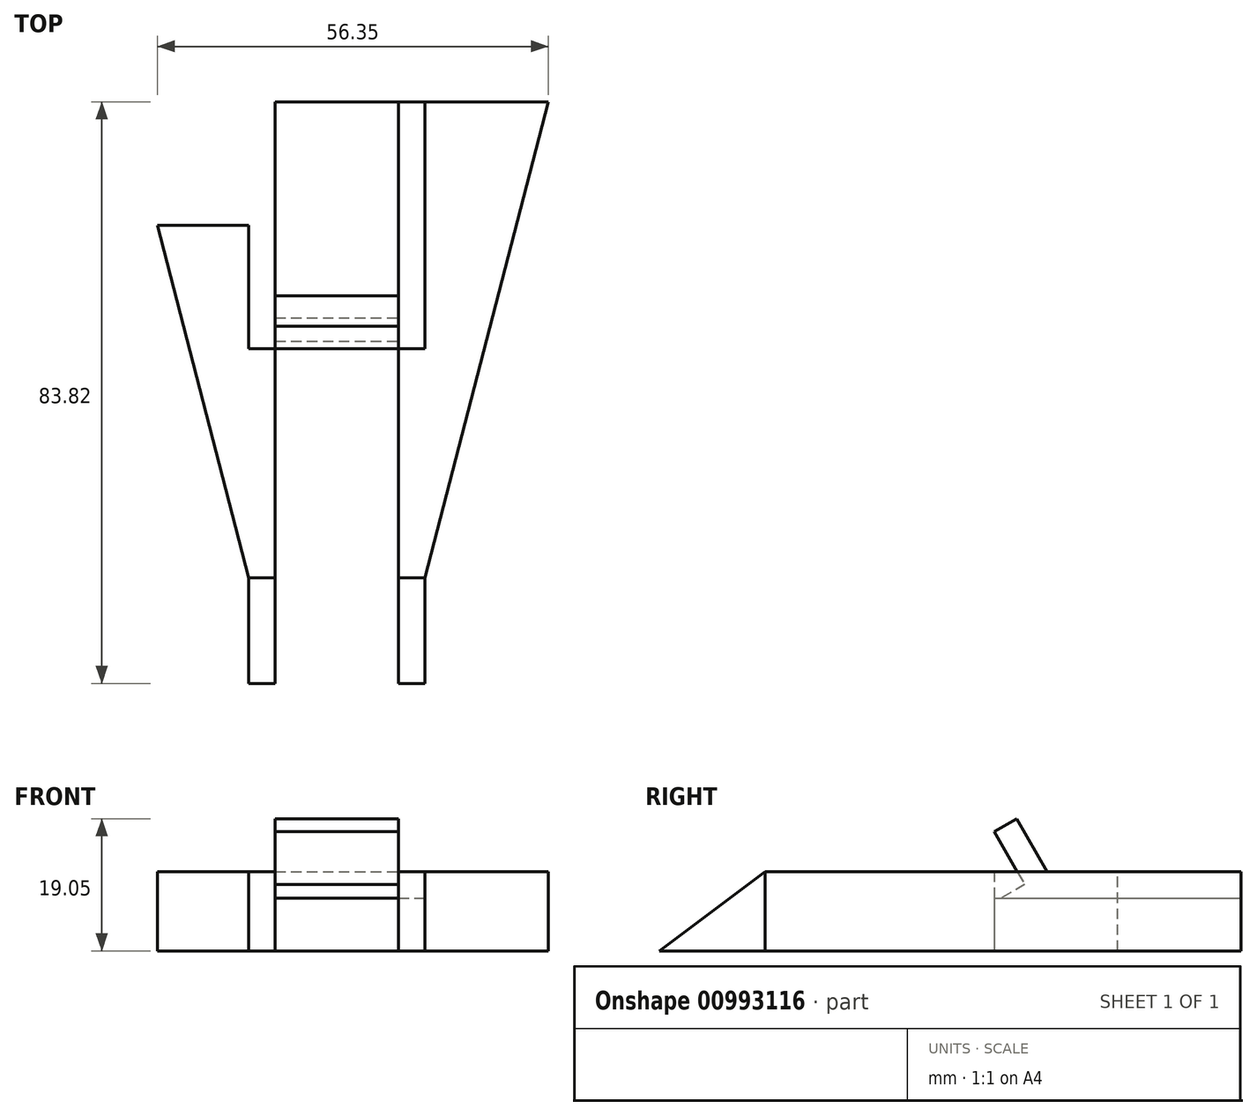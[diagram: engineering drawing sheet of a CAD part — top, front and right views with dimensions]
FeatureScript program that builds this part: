
annotation { "Feature Type Name" : "Feature", "Feature Type Description" : "" }
export const myFeature = defineFeature(function(context is Context, id is Id, definition is map)
    precondition{}
    {
        {
            var Q0;
            Q0=qCreatedBy(makeId("Top.planeOp"),FACE);
            var sketch = newSketch(context, id + "F0", { "sketchPlane" : qUnion([Q0])});
            skLineSegment(sketch, "E0.bottom", {"start": v(-79.84, -0.15) * mm, "end": v(-3.64, -0.15) * mm});
            skLineSegment(sketch, "E0.top", {"start": v(-79.84, -50.95) * mm, "end": v(-3.64, -50.95) * mm});
            skLineSegment(sketch, "E0.left", {"start": v(-79.84, -0.15) * mm, "end": v(-79.84, -50.95) * mm});
            skLineSegment(sketch, "E0.right", {"start": v(-3.64, -0.15) * mm, "end": v(-3.64, -50.95) * mm});
            skLineSegment(sketch, "E1.bottom", {"start": v(-54.44, -0.15) * mm, "end": v(-50.63, -0.15) * mm});
            skLineSegment(sketch, "E1.top", {"start": v(-54.44, -17.93) * mm, "end": v(-50.63, -17.93) * mm});
            skLineSegment(sketch, "E1.left", {"start": v(-54.44, -0.15) * mm, "end": v(-54.44, -17.93) * mm});
            skLineSegment(sketch, "E1.right", {"start": v(-50.63, -0.15) * mm, "end": v(-50.63, -17.93) * mm});
            skLineSegment(sketch, "E2.bottom", {"start": v(-32.85, -17.93) * mm, "end": v(-29.04, -17.93) * mm});
            skLineSegment(sketch, "E2.top", {"start": v(-32.85, -0.15) * mm, "end": v(-29.04, -0.15) * mm});
            skLineSegment(sketch, "E2.left", {"start": v(-32.85, -17.93) * mm, "end": v(-32.85, -0.15) * mm});
            skLineSegment(sketch, "E2.right", {"start": v(-29.04, -17.93) * mm, "end": v(-29.04, -0.15) * mm});
            skSolve(sketch);
        }
        {
            var Q0;
            Q0=makeQuery(id+"F0.imprint","IMPRINT",FACE,{"disambiguationData":[TD([[makeQuery(id+"F0.imprint","IMPRINT",EDGE,{"derivedFrom":sQuery(id+"F0.wireOp",EDGE,"E0.top")}),1.0]])]});
            extrude(context, id + "F1", {"entities" : qUnion([Q0]), "depth" : 3.8 * mm, "offsetDistance" : 25.4 * mm, "hasSecondDirection" : true, "secondDirectionOppositeDirection" : true, "secondDirectionDepth" : 7.62 * mm});
        }
        {
            var Q0;
            Q0=makeQuery(id+"F0.imprint","IMPRINT",FACE,{"disambiguationData":[TD([[makeQuery(id+"F0.imprint","IMPRINT",EDGE,{"derivedFrom":sQuery(id+"F0.wireOp",EDGE,"E1.bottom")}),-1.0]])]});
            var Q1;
            Q1=makeQuery(id+"F0.imprint","IMPRINT",FACE,{"disambiguationData":[TD([[makeQuery(id+"F0.imprint","IMPRINT",EDGE,{"derivedFrom":sQuery(id+"F0.wireOp",EDGE,"E2.bottom")}),1.0]])]});
            extrude(context, id + "F2", {"entities" : qUnion([Q0, Q1]), "operationType" : NewBodyOperationType.ADD, "oppositeDirection" : true, "depth" : 7.62 * mm, "offsetDistance" : 25.4 * mm});
        }
        {
            var Q0;
            Q0=makeQuery(id+"F1.opExtrude","CAP_FACE",FACE,{"disambiguationData":[OSD([sQuery(id+"F0.wireOp",EDGE,"E0.bottom"),sQuery(id+"F0.wireOp",EDGE,"E0.top"),sQuery(id+"F0.wireOp",EDGE,"E0.left"),sQuery(id+"F0.wireOp",EDGE,"E0.right"),sQuery(id+"F0.wireOp",EDGE,"E1.top"),sQuery(id+"F0.wireOp",EDGE,"E1.left"),sQuery(id+"F0.wireOp",EDGE,"E1.right"),sQuery(id+"F0.wireOp",EDGE,"E2.bottom"),sQuery(id+"F0.wireOp",EDGE,"E2.left"),sQuery(id+"F0.wireOp",EDGE,"E2.right")])],"isStart":false});
            var sketch = newSketch(context, id + "F3", { "sketchPlane" : qUnion([Q0])});
            skLineSegment(sketch, "E3.bottom", {"start": v(-50.63, -17.93) * mm, "end": v(-32.85, -17.93) * mm});
            skLineSegment(sketch, "E3.top", {"start": v(-50.63, -10.31) * mm, "end": v(-32.85, -10.31) * mm});
            skLineSegment(sketch, "E3.left", {"start": v(-50.63, -17.93) * mm, "end": v(-50.63, -10.31) * mm});
            skLineSegment(sketch, "E3.right", {"start": v(-32.85, -17.93) * mm, "end": v(-32.85, -10.31) * mm});
            skSolve(sketch);
        }
        {
            var Q0;
            Q0=makeQuery(id+"F3.imprint","IMPRINT",FACE,{"disambiguationData":[TD([[makeQuery(id+"F3.imprint","IMPRINT",EDGE,{"derivedFrom":sQuery(id+"F3.wireOp",EDGE,"E3.bottom")}),1.0]])]});
            extrude(context, id + "F4", {"entities" : qUnion([Q0]), "operationType" : NewBodyOperationType.ADD, "depth" : 7.62 * mm, "offsetDistance" : 25.4 * mm});
        }
        {
            var Q0;
            Q0=makeQuery(id+"F4.boolean.opBoolean","MERGE",FACE,{"derivedFrom":[makeQuery(id+"F1.opExtrude","SWEPT_FACE",FACE,{"disambiguationData":[OSD([sQuery(id+"F0.wireOp",EDGE,"E2.left")])]}),makeQuery(id+"F4.opExtrude","SWEPT_FACE",FACE,{"disambiguationData":[OSD([sQuery(id+"F3.wireOp",EDGE,"E3.right")])]})]});
            var sketch = newSketch(context, id + "F5", { "sketchPlane" : qUnion([Q0])});
            skLineSegment(sketch, "E4", {"start": v(-10.31, 3.81) * mm, "end": v(-14.71, 11.43) * mm});
            skLineSegment(sketch, "E5", {"start": v(-14.71, 11.43) * mm, "end": v(-17.93, 9.57) * mm});
            skLineSegment(sketch, "E6", {"start": v(-10.31, 3.8) * mm, "end": v(-13.53, 1.95) * mm});
            skLineSegment(sketch, "E7", {"start": v(-17.93, 9.57) * mm, "end": v(-13.53, 1.95) * mm});
            skLineSegment(sketch, "E8", {"start": v(-13.53, 1.95) * mm, "end": v(-16.91, 0) * mm});
            skSolve(sketch);
        }
        {
            var Q0;
            {var subQ0=sQuery(id+"F5.wireOp",EDGE,"E4");Q0=makeQuery(id+"F5.imprint","IMPRINT",FACE,{"disambiguationData":[TD([[makeQuery(id+"F5.imprint","IMPRINT",EDGE,{"derivedFrom":subQ0}),-1.0]])]});}
            var Q1;
            {var subQ0=sQuery(id+"F5.wireOp",EDGE,"E5");Q1=makeQuery(id+"F5.imprint","IMPRINT",FACE,{"disambiguationData":[TD([[makeQuery(id+"F5.imprint","IMPRINT",EDGE,{"derivedFrom":subQ0}),-1.0]])]});}
            var Q2;
            {var subQ5=sQuery(id+"F5.wireOp",EDGE,"E7");Q2=makeQuery(id+"F5.imprint","IMPRINT",FACE,{"disambiguationData":[TD([[makeQuery(id+"F5.imprint","IMPRINT",EDGE,{"derivedFrom":subQ5}),-1.0]])]});}
            extrude(context, id + "F6", {"entities" : qUnion([Q0, Q1, Q2]), "operationType" : NewBodyOperationType.REMOVE, "oppositeDirection" : true, "depth" : 17.78 * mm, "offsetDistance" : 25.4 * mm});
        }
        {
            var Q0;
            Q0=makeQuery(id+"F1.opExtrude","SWEPT_FACE",FACE,{"disambiguationData":[OSD([sQuery(id+"F0.wireOp",EDGE,"E0.top")])]});
            var sketch = newSketch(context, id + "F7", { "sketchPlane" : qUnion([Q0])});
            skLineSegment(sketch, "E9.bottom", {"start": v(-50.63, 3.8) * mm, "end": v(-32.85, 3.8) * mm});
            skLineSegment(sketch, "E9.top", {"start": v(-50.63, -7.62) * mm, "end": v(-32.85, -7.62) * mm});
            skLineSegment(sketch, "E9.left", {"start": v(-50.63, 3.8) * mm, "end": v(-50.63, -7.62) * mm});
            skLineSegment(sketch, "E9.right", {"start": v(-32.85, 3.8) * mm, "end": v(-32.85, -7.62) * mm});
            skSolve(sketch);
        }
        {
            var Q0;
            Q0=makeQuery(id+"F7.imprint","IMPRINT",FACE,{"disambiguationData":[TD([[makeQuery(id+"F7.imprint","IMPRINT",EDGE,{"derivedFrom":sQuery(id+"F7.wireOp",EDGE,"E9.bottom")}),-1.0]])]});
            extrude(context, id + "F8", {"entities" : qUnion([Q0]), "operationType" : NewBodyOperationType.REMOVE, "oppositeDirection" : true, "depth" : 33.02 * mm, "offsetDistance" : 25.4 * mm});
        }
        {
            var Q0;
            {var subQ0=sQuery(id+"F0.wireOp",EDGE,"E2.top");var subQ1=sQuery(id+"F0.wireOp",EDGE,"E1.bottom");var subQ2=sQuery(id+"F0.wireOp",EDGE,"E0.bottom");Q0=makeQuery(id+"F2.boolean.opBoolean","MERGE",FACE,{"derivedFrom":[makeQuery(id+"F1.opExtrude","SWEPT_FACE",FACE,{"disambiguationData":[OSD([subQ2]),TDD([makeQuery(id+"F0.imprint","IMPRINT",EDGE,{"disambiguationData":[TD([[makeQuery(id+"F0.imprint","INTERSECT",VERTEX,{"derivedFrom":[subQ2,sQuery(id+"F0.wireOp",EDGE,"E0.left")]}),-1.0]])],"derivedFrom":subQ2})])]}),makeQuery(id+"F1.opExtrude","SWEPT_FACE",FACE,{"disambiguationData":[OSD([subQ2]),TDD([makeQuery(id+"F0.imprint","IMPRINT",EDGE,{"disambiguationData":[TD([[makeQuery(id+"F0.imprint","INTERSECT",VERTEX,{"derivedFrom":[subQ2,subQ1,sQuery(id+"F0.wireOp",EDGE,"E1.right")]}),-1.0]])],"derivedFrom":subQ2})])]}),makeQuery(id+"F1.opExtrude","SWEPT_FACE",FACE,{"disambiguationData":[OSD([subQ2]),TDD([makeQuery(id+"F0.imprint","IMPRINT",EDGE,{"disambiguationData":[TD([[makeQuery(id+"F0.imprint","INTERSECT",VERTEX,{"derivedFrom":[subQ2,sQuery(id+"F0.wireOp",EDGE,"E0.right")]}),1.0]])],"derivedFrom":subQ2})])]}),makeQuery(id+"F2.opExtrude","SWEPT_FACE",FACE,{"disambiguationData":[OSD([subQ1])]}),makeQuery(id+"F2.opExtrude","SWEPT_FACE",FACE,{"disambiguationData":[OSD([subQ0])]})]});}
            extrude(context, id + "F9", {"entities" : qUnion([Q0]), "operationType" : NewBodyOperationType.ADD, "depth" : 17.78 * mm, "offsetDistance" : 25.4 * mm});
        }
        {
            var Q0;
            {var subQ3=sQuery(id+"F0.wireOp",EDGE,"E0.left");var subQ8=sQuery(id+"F0.wireOp",EDGE,"E0.top");Q0=makeQuery(id+"F8.boolean.opBoolean","SPLIT",FACE,{"disambiguationData":[TD([makeQuery(id+"F1.opExtrude","SWEPT_FACE",FACE,{"disambiguationData":[OSD([subQ3])]})])],"derivedFrom":makeQuery(id+"F1.opExtrude","SWEPT_FACE",FACE,{"disambiguationData":[OSD([subQ8])]})});}
            var sketch = newSketch(context, id + "F10", { "sketchPlane" : qUnion([Q0])});
            skLineSegment(sketch, "E10", {"start": v(-54.44, 3.8) * mm, "end": v(-54.44, -7.62) * mm});
            skSolve(sketch);
        }
        {
            var Q0;
            {var subQ0=sQuery(id+"F10.wireOp",EDGE,"E10");Q0=makeQuery(id+"F10.imprint","IMPRINT",FACE,{"disambiguationData":[TD([[makeQuery(id+"F10.imprint","IMPRINT",EDGE,{"derivedFrom":subQ0}),1.0]])]});}
            extrude(context, id + "F11", {"entities" : qUnion([Q0]), "operationType" : NewBodyOperationType.ADD, "depth" : 15.24 * mm, "offsetDistance" : 25.4 * mm});
        }
        {
            var Q0;
            {var subQ3=sQuery(id+"F0.wireOp",EDGE,"E0.right");var subQ8=sQuery(id+"F0.wireOp",EDGE,"E0.top");Q0=makeQuery(id+"F8.boolean.opBoolean","SPLIT",FACE,{"disambiguationData":[TD([makeQuery(id+"F1.opExtrude","SWEPT_FACE",FACE,{"disambiguationData":[OSD([subQ3])]})])],"derivedFrom":makeQuery(id+"F1.opExtrude","SWEPT_FACE",FACE,{"disambiguationData":[OSD([subQ8])]})});}
            var sketch = newSketch(context, id + "F12", { "sketchPlane" : qUnion([Q0])});
            skLineSegment(sketch, "E11", {"start": v(-29.04, 3.8) * mm, "end": v(-29.04, -7.62) * mm});
            skSolve(sketch);
        }
        {
            var Q0;
            {var subQ0=sQuery(id+"F12.wireOp",EDGE,"E11");Q0=makeQuery(id+"F12.imprint","IMPRINT",FACE,{"disambiguationData":[TD([[makeQuery(id+"F12.imprint","IMPRINT",EDGE,{"derivedFrom":subQ0}),-1.0]])]});}
            extrude(context, id + "F13", {"entities" : qUnion([Q0]), "operationType" : NewBodyOperationType.ADD, "depth" : 15.24 * mm, "offsetDistance" : 25.4 * mm});
        }
        {
            var Q0;
            Q0=makeQuery(id+"F11.opExtrude","SWEPT_FACE",FACE,{"disambiguationData":[OSD([sQuery(id+"F10.wireOp",EDGE,"E10")])]});
            var sketch = newSketch(context, id + "F14", { "sketchPlane" : qUnion([Q0])});
            skLineSegment(sketch, "E12", {"start": v(50.95, 3.81) * mm, "end": v(66.2, -7.62) * mm});
            skSolve(sketch);
        }
        {
            var Q0;
            Q0=makeQuery(id+"F14.imprint","IMPRINT",FACE,{"disambiguationData":[TD([[makeQuery(id+"F14.imprint","IMPRINT",EDGE,{"derivedFrom":sQuery(id+"F14.wireOp",EDGE,"E12")}),1.0]])]});
            extrude(context, id + "F15", {"entities" : qUnion([Q0]), "operationType" : NewBodyOperationType.REMOVE, "oppositeDirection" : true, "depth" : 25.4 * mm, "offsetDistance" : 25.4 * mm});
        }
        {
            var Q0;
            {var subQ0=sQuery(id+"F0.wireOp",EDGE,"E2.right");var subQ1=sQuery(id+"F0.wireOp",EDGE,"E2.left");var subQ2=sQuery(id+"F0.wireOp",EDGE,"E2.bottom");var subQ3=sQuery(id+"F0.wireOp",EDGE,"E1.right");var subQ4=sQuery(id+"F0.wireOp",EDGE,"E1.left");var subQ5=sQuery(id+"F0.wireOp",EDGE,"E1.top");var subQ6=sQuery(id+"F0.wireOp",EDGE,"E0.right");var subQ7=sQuery(id+"F0.wireOp",EDGE,"E0.left");var subQ8=sQuery(id+"F0.wireOp",EDGE,"E0.top");var subQ9=sQuery(id+"F0.wireOp",EDGE,"E0.bottom");var subQ10=makeQuery(id+"F1.opExtrude","CAP_FACE",FACE,{"disambiguationData":[OSD([subQ9,subQ8,subQ7,subQ6,subQ5,subQ4,subQ3,subQ2,subQ1,subQ0])],"isStart":false});var subQ11=sQuery(id+"F7.wireOp",EDGE,"E9.left");var subQ13=makeQuery(id+"F1.opExtrude","SWEPT_FACE",FACE,{"disambiguationData":[OSD([subQ8])]});var subQ14=makeQuery(id+"F1.opExtrude","SWEPT_FACE",FACE,{"disambiguationData":[OSD([subQ7])]});var subQ15=makeQuery(id+"F8.boolean.opBoolean","SPLIT",EDGE,{"disambiguationData":[TD([subQ14])],"derivedFrom":makeQuery(id+"F1.opExtrude","CAP_EDGE",EDGE,{"disambiguationData":[OSD([subQ8])],"isStart":false})});var subQ17=makeQuery(id+"F0.imprint","IMPRINT",EDGE,{"disambiguationData":[TD([[makeQuery(id+"F0.imprint","INTERSECT",VERTEX,{"derivedFrom":[subQ9,subQ7]}),-1.0]])],"derivedFrom":subQ9});Q0=makeQuery(id+"F11.boolean.opBoolean","MERGE",FACE,{"derivedFrom":[makeQuery(id+"F9.boolean.opBoolean","MERGE",FACE,{"derivedFrom":[makeQuery(id+"F8.boolean.opBoolean","SPLIT",FACE,{"disambiguationData":[TD([subQ14])],"derivedFrom":makeQuery(id+"F4.boolean.opBoolean","SPLIT",FACE,{"disambiguationData":[TD([subQ13])],"derivedFrom":subQ10})}),makeQuery(id+"F9.opExtrude","SWEPT_FACE",FACE,{"disambiguationData":[OSD([subQ9]),TDD([makeQuery(id+"F1.opExtrude","CAP_EDGE",EDGE,{"disambiguationData":[OSD([subQ9]),TDD([subQ17])],"isStart":false})])]})]}),makeQuery(id+"F11.opExtrude","SWEPT_FACE",FACE,{"disambiguationData":[OSD([subQ8]),TDD([makeQuery(id+"F10.imprint","IMPRINT",EDGE,{"disambiguationData":[TD([[makeQuery(id+"F10.imprint","INTERSECT",VERTEX,{"derivedFrom":[makeQuery(id+"F8.boolean.opBoolean","COPY",EDGE,{"derivedFrom":makeQuery(id+"F8.opExtrude","CAP_EDGE",EDGE,{"disambiguationData":[OSD([subQ11])],"isStart":true})}),subQ15]}),1.0]])],"derivedFrom":subQ15})])]})]});}
            var sketch = newSketch(context, id + "F16", { "sketchPlane" : qUnion([Q0])});
            skLineSegment(sketch, "E13", {"start": v(-72.22, 17.63) * mm, "end": v(-54.44, -50.95) * mm});
            skSolve(sketch);
        }
        {
            var Q0;
            {var subQ0=sQuery(id+"F0.wireOp",EDGE,"E2.right");var subQ1=sQuery(id+"F0.wireOp",EDGE,"E2.left");var subQ2=sQuery(id+"F0.wireOp",EDGE,"E2.bottom");var subQ3=sQuery(id+"F0.wireOp",EDGE,"E1.right");var subQ4=sQuery(id+"F0.wireOp",EDGE,"E1.left");var subQ5=sQuery(id+"F0.wireOp",EDGE,"E1.top");var subQ6=sQuery(id+"F0.wireOp",EDGE,"E0.right");var subQ7=sQuery(id+"F0.wireOp",EDGE,"E0.left");var subQ8=sQuery(id+"F0.wireOp",EDGE,"E0.top");var subQ9=sQuery(id+"F0.wireOp",EDGE,"E0.bottom");var subQ10=makeQuery(id+"F1.opExtrude","CAP_FACE",FACE,{"disambiguationData":[OSD([subQ9,subQ8,subQ7,subQ6,subQ5,subQ4,subQ3,subQ2,subQ1,subQ0])],"isStart":false});var subQ11=makeQuery(id+"F1.opExtrude","SWEPT_FACE",FACE,{"disambiguationData":[OSD([subQ6])]});var subQ12=makeQuery(id+"F1.opExtrude","SWEPT_FACE",FACE,{"disambiguationData":[OSD([subQ8])]});var subQ13=sQuery(id+"F7.wireOp",EDGE,"E9.right");var subQ15=makeQuery(id+"F8.boolean.opBoolean","SPLIT",EDGE,{"disambiguationData":[TD([subQ11])],"derivedFrom":makeQuery(id+"F1.opExtrude","CAP_EDGE",EDGE,{"disambiguationData":[OSD([subQ8])],"isStart":false})});var subQ17=makeQuery(id+"F0.imprint","IMPRINT",EDGE,{"disambiguationData":[TD([[makeQuery(id+"F0.imprint","INTERSECT",VERTEX,{"derivedFrom":[subQ9,subQ6]}),1.0]])],"derivedFrom":subQ9});Q0=makeQuery(id+"F13.boolean.opBoolean","MERGE",FACE,{"derivedFrom":[makeQuery(id+"F9.boolean.opBoolean","MERGE",FACE,{"derivedFrom":[makeQuery(id+"F8.boolean.opBoolean","SPLIT",FACE,{"disambiguationData":[TD([subQ11])],"derivedFrom":makeQuery(id+"F4.boolean.opBoolean","SPLIT",FACE,{"disambiguationData":[TD([subQ12])],"derivedFrom":subQ10})}),makeQuery(id+"F9.opExtrude","SWEPT_FACE",FACE,{"disambiguationData":[OSD([subQ9]),TDD([makeQuery(id+"F1.opExtrude","CAP_EDGE",EDGE,{"disambiguationData":[OSD([subQ9]),TDD([subQ17])],"isStart":false})])]})]}),makeQuery(id+"F13.opExtrude","SWEPT_FACE",FACE,{"disambiguationData":[OSD([subQ8]),TDD([makeQuery(id+"F12.imprint","IMPRINT",EDGE,{"disambiguationData":[TD([[makeQuery(id+"F12.imprint","INTERSECT",VERTEX,{"derivedFrom":[makeQuery(id+"F8.boolean.opBoolean","COPY",EDGE,{"derivedFrom":makeQuery(id+"F8.opExtrude","CAP_EDGE",EDGE,{"disambiguationData":[OSD([subQ13])],"isStart":true})}),subQ15]}),-1.0]])],"derivedFrom":subQ15})])]})]});}
            var sketch = newSketch(context, id + "F17", { "sketchPlane" : qUnion([Q0])});
            skLineSegment(sketch, "E14", {"start": v(-11.26, 17.63) * mm, "end": v(-29.04, -50.95) * mm});
            skSolve(sketch);
        }
        {
            var Q0;
            Q0=makeQuery(id+"F16.imprint","IMPRINT",FACE,{"disambiguationData":[TD([[makeQuery(id+"F16.imprint","IMPRINT",EDGE,{"derivedFrom":sQuery(id+"F16.wireOp",EDGE,"nTniuorG-mLos-qBTP-dhj2-vk5b24vMcQWH")}),1.0]])]});
            var Q1;
            Q1=makeQuery(id+"F17.imprint","IMPRINT",FACE,{"disambiguationData":[TD([[makeQuery(id+"F17.imprint","IMPRINT",EDGE,{"derivedFrom":sQuery(id+"F17.wireOp",EDGE,"ubrkWLQK-j7pI-iAjC-EHIu-Fce79rrTo383")}),-1.0]])]});
            var Q2;
            {var subQ0=sQuery(id+"F16.wireOp",EDGE,"E13");Q2=makeQuery(id+"F16.imprint","IMPRINT",FACE,{"disambiguationData":[TD([[makeQuery(id+"F16.imprint","IMPRINT",EDGE,{"derivedFrom":subQ0}),-1.0]])]});}
            var Q3;
            {var subQ0=sQuery(id+"F17.wireOp",EDGE,"E14");Q3=makeQuery(id+"F17.imprint","IMPRINT",FACE,{"disambiguationData":[TD([[makeQuery(id+"F17.imprint","IMPRINT",EDGE,{"derivedFrom":subQ0}),1.0]])]});}
            extrude(context, id + "F18", {"entities" : qUnion([Q0, Q1, Q2, Q3]), "operationType" : NewBodyOperationType.REMOVE, "oppositeDirection" : true, "depth" : 25.4 * mm, "offsetDistance" : 25.4 * mm});
        }
    });
